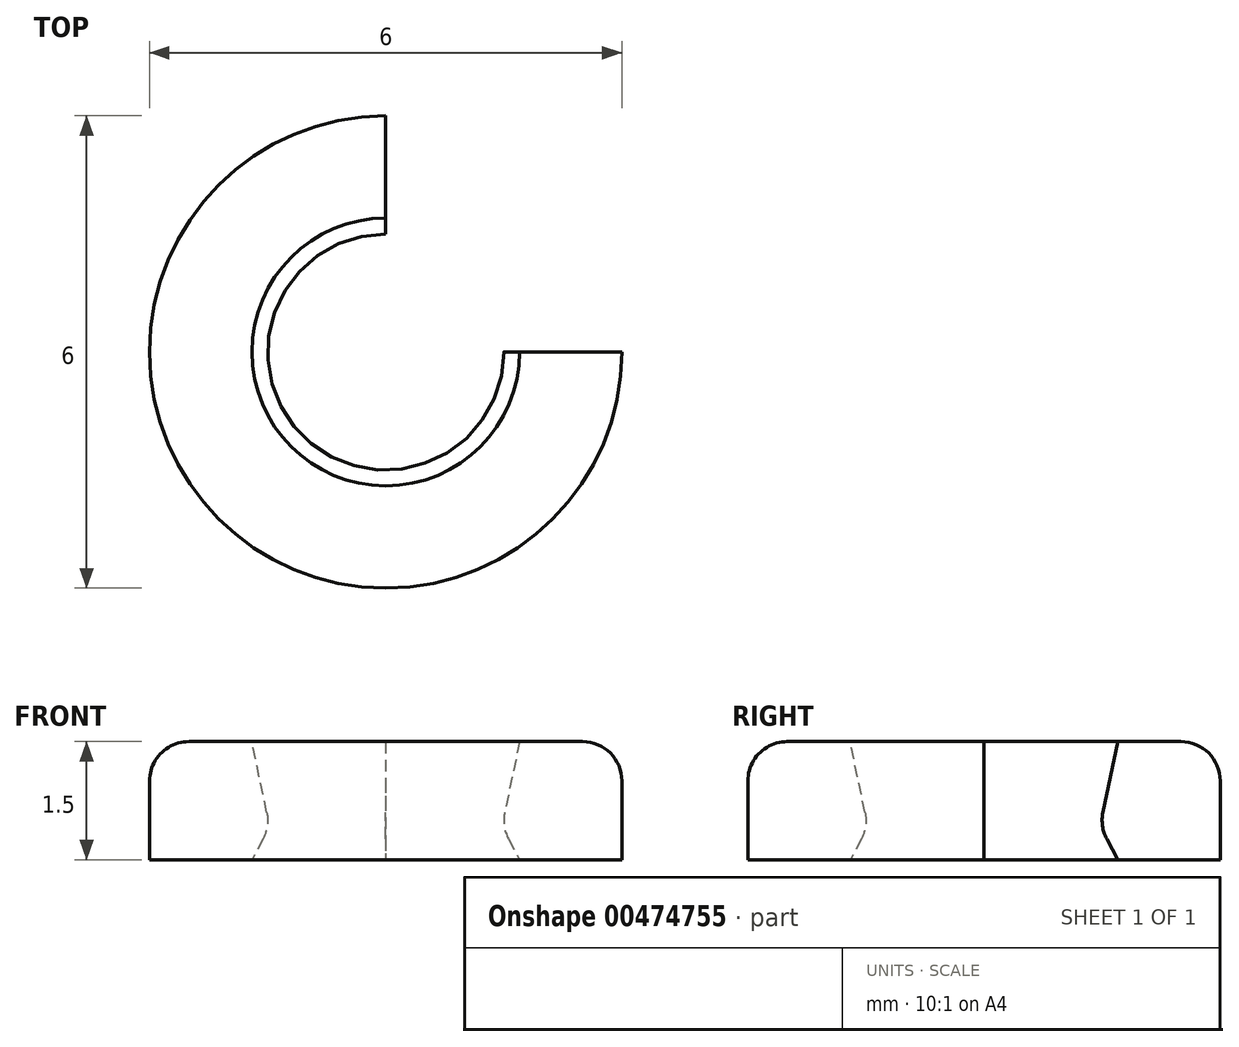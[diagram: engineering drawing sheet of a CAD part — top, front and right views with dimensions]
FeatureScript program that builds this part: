
annotation { "Feature Type Name" : "Feature", "Feature Type Description" : "" }
export const myFeature = defineFeature(function(context is Context, id is Id, definition is map)
    precondition{}
    {
        {
            var Q0;
            Q0=qCreatedBy(makeId("Top.planeOp"),FACE);
            var sketch = newSketch(context, id + "F0", { "sketchPlane" : qUnion([Q0])});
            skArc(sketch, "E0", {"start": v(0, 3) * mm, "mid": v(-2.12, -2.12) * mm, "end": v(3, 0) * mm});
            skArc(sketch, "E1", {"start": v(0, 1.5) * mm, "mid": v(-1.06, -1.06) * mm, "end": v(1.5, 0) * mm});
            skLineSegment(sketch, "E2", {"start": v(0, 1.5) * mm, "end": v(0, 3) * mm});
            skLineSegment(sketch, "E3", {"start": v(1.5, 0) * mm, "end": v(3, 0) * mm});
            skSolve(sketch);
        }
        {
            var Q0;
            Q0 = qSketchRegion(id + "F0", true);
            extrude(context, id + "F1", {"entities" : qUnion([Q0]), "depth" : 1.5 * mm, "offsetDistance" : 25 * mm});
        }
        {
            var Q0;
            Q0=makeQuery(id+"F1.opExtrude","SWEPT_FACE",FACE,{"disambiguationData":[OSD([sQuery(id+"F0.wireOp",EDGE,"E2")])]});
            var sketch = newSketch(context, id + "F2", { "sketchPlane" : qUnion([Q0])});
            skLineSegment(sketch, "E4", {"start": v(1.5, 1.5) * mm, "end": v(1.7, 1.5) * mm});
            skLineSegment(sketch, "E5", {"start": v(0, 0) * mm, "end": v(0, 1.5) * mm, "construction": true});
            skLineSegment(sketch, "E6", {"start": v(1.7, 1.5) * mm, "end": v(1.51, 0.6) * mm});
            skLineSegment(sketch, "E7", {"start": v(1.5, 0) * mm, "end": v(1.7, 0) * mm});
            skLineSegment(sketch, "E8", {"start": v(1.7, 0) * mm, "end": v(1.56, 0.26) * mm});
            skArc(sketch, "E9", {"start": v(1.51, 0.6) * mm, "mid": v(1.5, 0.43) * mm, "end": v(1.56, 0.26) * mm});
            skLineSegment(sketch, "E10", {"start": v(1.5, 1.5) * mm, "end": v(1.5, 0) * mm});
            skSolve(sketch);
        }
        {
            var Q0;
            Q0 = qSketchRegion(id + "F2", true);
            var Q1;
            Q1=sQuery(id+"F2.wireOp",EDGE,"E5");
            revolve(context, id + "F3", {"operationType" : NewBodyOperationType.REMOVE, "entities" : qUnion([Q0]), "axis" : qUnion([Q1]), "revolveType" : RevolveType.FULL, "oppositeDirection" : true});
        }
        {
            var Q0;
            Q0=makeQuery(id+"F1.opExtrude","CAP_EDGE",EDGE,{"disambiguationData":[OSD([sQuery(id+"F0.wireOp",EDGE,"E0")])],"isStart":false});
            fillet(context, id + "F4", {"entities" : qUnion([Q0]), "radius" : 0.5 * mm, "tangentPropagation" : true, "allowEdgeOverflow" : false});
        }
    });
